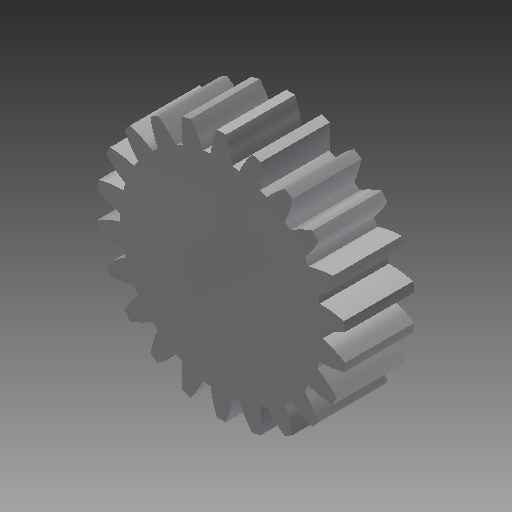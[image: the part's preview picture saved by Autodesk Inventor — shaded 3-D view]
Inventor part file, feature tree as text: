
AUTODESK INVENTOR PART (.ipt)
format: ipt  version: 2019 (Build 230136000, 136)  size: 230,912 bytes
history: native  units: mm (DEFAULTED — no unit token found)
features: plane x3, other x3, sketch x2, extrude x1
ambient origin geometry x8: Origin, YZ Plane, XZ Plane, XY Plane, X Axis, Y Axis, Z Axis, Center Point
bodies: Solid1 (feature_tree)
feature tree (9):
  extrude  "Extrusion1"  Depth=10.0mm TaperAngle=0.0deg
  plane  "Work Plane2"
  plane  "Work Plane8"
  plane  "Work Plane9"
  other  "正齒輪"
  sketch  "Sketch1"  dims[d0=35.980829mm d1=10.0mm d2=0.0mm]
  sketch  "Sketch2"  dims[d3=33.257759mm d4=10.0mm d5=0.0mm d16=43.083915mm d17=0.0mm d34=1.427997mm d39=0.0mm d41=0.0mm d43=43.083915mm d46=43.083915mm d47=0.0mm d48=0.0mm]
  other  "Srf1"
  other  "節圓直徑"
